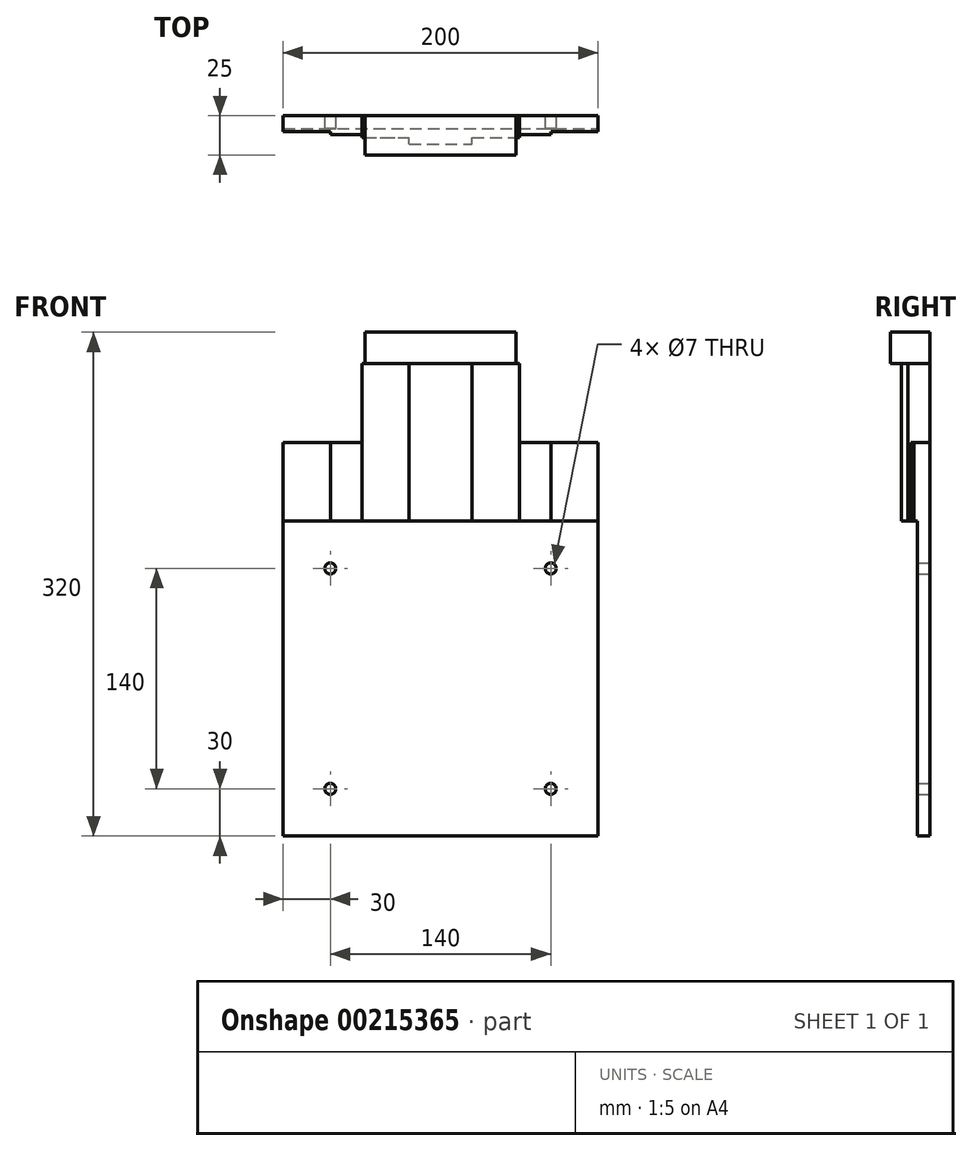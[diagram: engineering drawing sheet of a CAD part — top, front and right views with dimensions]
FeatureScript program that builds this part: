
annotation { "Feature Type Name" : "Feature", "Feature Type Description" : "" }
export const myFeature = defineFeature(function(context is Context, id is Id, definition is map)
    precondition{}
    {
        {
            var Q0;
            Q0=qCreatedBy(makeId("Front.planeOp"),FACE);
            var sketch = newSketch(context, id + "F0", { "sketchPlane" : qUnion([Q0])});
            skLineSegment(sketch, "E0.bottom", {"start": v(-100, 100) * mm, "end": v(100, 100) * mm});
            skLineSegment(sketch, "E0.top", {"start": v(-100, -100) * mm, "end": v(100, -100) * mm});
            skLineSegment(sketch, "E0.left", {"start": v(-100, 100) * mm, "end": v(-100, -100) * mm});
            skLineSegment(sketch, "E0.right", {"start": v(100, 100) * mm, "end": v(100, -100) * mm});
            skPoint(sketch, "E0.middle", {"position": v(0, 0) * mm});
            skLineSegment(sketch, "E1.bottom", {"start": v(-100, 100) * mm, "end": v(-50, 100) * mm});
            skLineSegment(sketch, "E1.top", {"start": v(-100, 150) * mm, "end": v(-50, 150) * mm});
            skLineSegment(sketch, "E1.left", {"start": v(-100, 100) * mm, "end": v(-100, 150) * mm});
            skLineSegment(sketch, "E1.right", {"start": v(-50, 100) * mm, "end": v(-50, 150) * mm});
            skLineSegment(sketch, "E2.MirrorCS", {"start": v(100, 150) * mm, "end": v(50, 150) * mm});
            skLineSegment(sketch, "E3.MirrorCS", {"start": v(100, 100) * mm, "end": v(100, 150) * mm});
            skLineSegment(sketch, "E4.MirrorCS", {"start": v(50, 100) * mm, "end": v(50, 150) * mm});
            skLineSegment(sketch, "E5", {"start": v(-50, 150) * mm, "end": v(50, 150) * mm});
            skPoint(sketch, "E6", {"position": v(-50, 150) * mm});
            skPoint(sketch, "E7.endSnap0", {"position": v(0, 150) * mm});
            skLineSegment(sketch, "E8", {"start": v(-50, 150) * mm, "end": v(-50, 200) * mm});
            skLineSegment(sketch, "E9.MirrorCS", {"start": v(50, 150) * mm, "end": v(50, 200) * mm});
            skLineSegment(sketch, "E10", {"start": v(-50, 200) * mm, "end": v(50, 200) * mm});
            skLineSegment(sketch, "E11", {"start": v(-20, 150) * mm, "end": v(-20, 200) * mm});
            skLineSegment(sketch, "E12", {"start": v(-20, 200) * mm, "end": v(-20, 100) * mm});
            skLineSegment(sketch, "E13", {"start": v(20, 200) * mm, "end": v(20, 100) * mm});
            skLineSegment(sketch, "E14", {"start": v(-70, 100) * mm, "end": v(-70, 150) * mm});
            skLineSegment(sketch, "E15", {"start": v(70, 100) * mm, "end": v(70, 150) * mm});
            skCircle(sketch, "E16", {"center": v(-70, 70) * mm, "radius": 3.5 * mm});
            skLineSegment(sketch, "E17", {"start": v(0, 0) * mm, "end": v(0, 26.3) * mm});
            skCircle(sketch, "E18", {"center": v(-70, -70) * mm, "radius": 3.5 * mm});
            skCircle(sketch, "E19.MirrorC", {"center": v(70, -70) * mm, "radius": 3.5 * mm});
            skCircle(sketch, "E20.MirrorC", {"center": v(70, 70) * mm, "radius": 3.5 * mm});
            skLineSegment(sketch, "E21.bottom", {"start": v(-48, 220) * mm, "end": v(48, 220) * mm});
            skPoint(sketch, "E21.middle", {"position": v(0, 200) * mm});
            skLineSegment(sketch, "E22", {"start": v(-48, 200) * mm, "end": v(48, 200) * mm});
            skLineSegment(sketch, "E23", {"start": v(48, 200) * mm, "end": v(48, 220) * mm});
            skLineSegment(sketch, "E24", {"start": v(-48, 200) * mm, "end": v(-48, 220) * mm});
            skSolve(sketch);
        }
        {
            var Q0;
            Q0=makeQuery(id+"F0.imprint","IMPRINT",FACE,{"disambiguationData":[TD([[makeQuery(id+"F0.imprint","IMPRINT",EDGE,{"derivedFrom":sQuery(id+"F0.wireOp",EDGE,"E0.top")}),1.0]])]});
            extrude(context, id + "F1", {"entities" : qUnion([Q0]), "depth" : 8 * mm});
        }
        {
            var Q0;
            {var subQ0=sQuery(id+"F0.wireOp",EDGE,"E1.left");Q0=makeQuery(id+"F0.imprint","IMPRINT",FACE,{"disambiguationData":[TD([[makeQuery(id+"F0.imprint","IMPRINT",EDGE,{"derivedFrom":subQ0}),-1.0]])]});}
            var Q1;
            {var subQ0=sQuery(id+"F0.wireOp",EDGE,"E3.MirrorCS");Q1=makeQuery(id+"F0.imprint","IMPRINT",FACE,{"disambiguationData":[TD([[makeQuery(id+"F0.imprint","IMPRINT",EDGE,{"derivedFrom":subQ0}),1.0]])]});}
            extrude(context, id + "F2", {"entities" : qUnion([Q0, Q1]), "operationType" : NewBodyOperationType.ADD, "depth" : 10 * mm});
        }
        {
            var Q0;
            {var subQ0=sQuery(id+"F0.wireOp",EDGE,"E1.right");Q0=makeQuery(id+"F0.imprint","IMPRINT",FACE,{"disambiguationData":[TD([[makeQuery(id+"F0.imprint","IMPRINT",EDGE,{"derivedFrom":subQ0}),1.0]])]});}
            var Q1;
            {var subQ0=sQuery(id+"F0.wireOp",EDGE,"E4.MirrorCS");Q1=makeQuery(id+"F0.imprint","IMPRINT",FACE,{"disambiguationData":[TD([[makeQuery(id+"F0.imprint","IMPRINT",EDGE,{"derivedFrom":subQ0}),-1.0]])]});}
            extrude(context, id + "F3", {"entities" : qUnion([Q0, Q1]), "operationType" : NewBodyOperationType.ADD, "depth" : 12 * mm});
        }
        {
            var Q0;
            {var subQ0=sQuery(id+"F0.wireOp",EDGE,"E1.right");Q0=makeQuery(id+"F0.imprint","IMPRINT",FACE,{"disambiguationData":[TD([[makeQuery(id+"F0.imprint","IMPRINT",EDGE,{"derivedFrom":subQ0}),-1.0]])]});}
            var Q1;
            {var subQ0=sQuery(id+"F0.wireOp",EDGE,"E4.MirrorCS");Q1=makeQuery(id+"F0.imprint","IMPRINT",FACE,{"disambiguationData":[TD([[makeQuery(id+"F0.imprint","IMPRINT",EDGE,{"derivedFrom":subQ0}),1.0]])]});}
            var Q2;
            {var subQ0=sQuery(id+"F0.wireOp",EDGE,"E8");Q2=makeQuery(id+"F0.imprint","IMPRINT",FACE,{"disambiguationData":[TD([[makeQuery(id+"F0.imprint","IMPRINT",EDGE,{"derivedFrom":subQ0}),-1.0]])]});}
            var Q3;
            {var subQ0=sQuery(id+"F0.wireOp",EDGE,"E9.MirrorCS");Q3=makeQuery(id+"F0.imprint","IMPRINT",FACE,{"disambiguationData":[TD([[makeQuery(id+"F0.imprint","IMPRINT",EDGE,{"derivedFrom":subQ0}),1.0]])]});}
            extrude(context, id + "F4", {"entities" : qUnion([Q0, Q1, Q2, Q3]), "operationType" : NewBodyOperationType.ADD, "depth" : 14 * mm});
        }
        {
            var Q0;
            {var subQ0=sQuery(id+"F0.wireOp",EDGE,"E12");var subQ1=sQuery(id+"F0.wireOp",EDGE,"E0.bottom");var subQ2=makeQuery(id+"F0.imprint","INTERSECT",VERTEX,{"derivedFrom":[subQ1,subQ0]});Q0=makeQuery(id+"F0.imprint","IMPRINT",FACE,{"disambiguationData":[TD([[makeQuery(id+"F0.imprint","IMPRINT",EDGE,{"disambiguationData":[TD([[subQ2,-1.0]])],"derivedFrom":subQ1}),1.0]])]});}
            var Q1;
            {var subQ0=sQuery(id+"F0.wireOp",EDGE,"E12");var subQ1=sQuery(id+"F0.wireOp",EDGE,"E5");var subQ2=makeQuery(id+"F0.imprint","INTERSECT",VERTEX,{"derivedFrom":[subQ1,subQ0]});Q1=makeQuery(id+"F0.imprint","IMPRINT",FACE,{"disambiguationData":[TD([[makeQuery(id+"F0.imprint","IMPRINT",EDGE,{"disambiguationData":[TD([[subQ2,-1.0]])],"derivedFrom":subQ1}),1.0]])]});}
            extrude(context, id + "F5", {"entities" : qUnion([Q0, Q1]), "operationType" : NewBodyOperationType.ADD, "depth" : 18 * mm});
        }
        {
            var Q0;
            Q0=makeQuery(id+"F0.imprint","IMPRINT",FACE,{"disambiguationData":[TD([[makeQuery(id+"F0.imprint","IMPRINT",EDGE,{"derivedFrom":sQuery(id+"F0.wireOp",EDGE,"E21.bottom")}),-1.0]])]});
            extrude(context, id + "F6", {"entities" : qUnion([Q0]), "operationType" : NewBodyOperationType.ADD, "depth" : 25 * mm});
        }
    });
